# Revit family: Hydrant_Wall_Narrow-Zurn-Z1349
name_source: partatom
category: Plumbing Fixtures
units: mm (PartAtom-declared; Revit-internal decimal feet)

## family parameters
Cut with Voids When Loaded = No
Host = Face
Maintain Annotation Orientation = No
OmniClass Number = 23.65.70.14.11.11
OmniClass Title = Security Drinking Fountains/Coolers
Part Type = Normal
Room Calculation Point = No
Round Connector Dimension = Use Radius
Shared = No

## types (1)
- Z1349 Narrow Wall Hydrant
    Approx. Weight (Lbs) = 2 "
    Assembly Code = D2020100
    Body Height of Wall Hydrant = 5.5 "
    CW Connection = Yes
    CWFU = 1
    Default Elevation = 20 "
    Description = Narrow Wall Hydrant
    Dim_A = 2 "
    Duct Size = 1.313 "
    Female Inlet Connector = 0.75 "
    Female Inlet Connector Radius = 0.375 "
    HW Connection = No
    HWFU = 0
    Height of Plate = 4.813 "
    Main Material = Bronze - Zurn - Polished
    Male Hose Connector = 0.75 "
    Male Hose Connector Radius = 0.375 "
    Manufacturer = Zurn Water, LLC
    Manufacurer Brand = Zurn
    Model = Z1349
    Modified Date = 01/23/2026
    Narrow wall = Steel - Zurn - Stainless - Polished
    Product Documentation Link = https://files.zurn.com
    Product Installation Sheet URL = https://files.zurn.com
    Product Page URL = https://www.zurn.com
    URL = www.zurn.com
    Vent Connection = No
    WFU = 0
    Waste Connection = No
    Width of Plate = 3.125 "

## geometry (parser evidence)
native form markers: Blend x4, Sweep x2
no freeform markers — native parametric forms only
